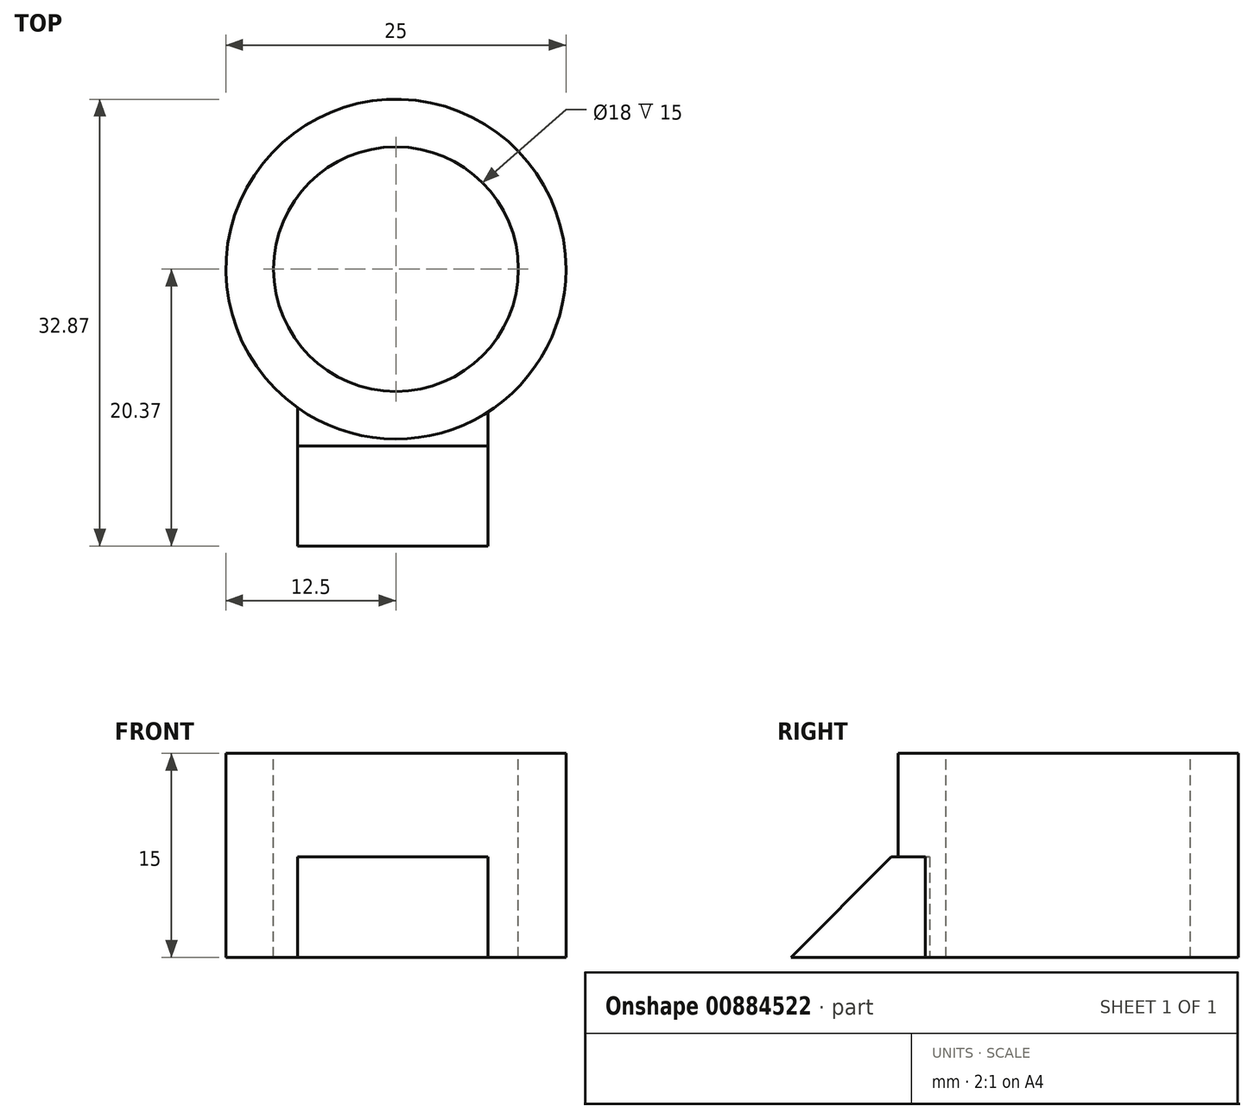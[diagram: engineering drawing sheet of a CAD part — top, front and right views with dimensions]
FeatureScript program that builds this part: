
annotation { "Feature Type Name" : "Feature", "Feature Type Description" : "" }
export const myFeature = defineFeature(function(context is Context, id is Id, definition is map)
    precondition{}
    {
        {
            var Q0;
            Q0=qCreatedBy(makeId("Top.planeOp"),FACE);
            var sketch = newSketch(context, id + "F0", { "sketchPlane" : qUnion([Q0])});
            skCircle(sketch, "E0", {"center": v(0, 0) * mm, "radius": 12.5 * mm});
            skSolve(sketch);
        }
        {
            var Q0;
            Q0 = qSketchRegion(id + "F0", true);
            extrude(context, id + "F1", {"entities" : qUnion([Q0]), "endBound" : BoundingType.SYMMETRIC, "depth" : 15 * mm, "offsetDistance" : 25 * mm});
        }
        {
            var Q0;
            Q0=makeQuery(id+"F1.opExtrude","CAP_FACE",FACE,{"disambiguationData":[OSD([sQuery(id+"F0.wireOp",EDGE,"E0")])],"isStart":false});
            var sketch = newSketch(context, id + "F2", { "sketchPlane" : qUnion([Q0])});
            skCircle(sketch, "E1", {"center": v(0, 0) * mm, "radius": 9 * mm});
            skSolve(sketch);
        }
        {
            var Q0;
            Q0 = qSketchRegion(id + "F2", true);
            extrude(context, id + "F3", {"entities" : qUnion([Q0]), "operationType" : NewBodyOperationType.REMOVE, "oppositeDirection" : true, "depth" : 25 * mm, "offsetDistance" : 25 * mm});
        }
        {
            var Q0;
            Q0=qCreatedBy(makeId("Front.planeOp"),FACE);
            var sketch = newSketch(context, id + "F4", { "sketchPlane" : qUnion([Q0])});
            skLineSegment(sketch, "E2.bottom", {"start": v(-7.23, -0.13) * mm, "end": v(6.77, -0.13) * mm});
            skLineSegment(sketch, "E2.top", {"start": v(-7.23, -7.5) * mm, "end": v(6.77, -7.5) * mm});
            skLineSegment(sketch, "E2.left", {"start": v(-7.23, -0.13) * mm, "end": v(-7.23, -7.5) * mm});
            skLineSegment(sketch, "E2.right", {"start": v(6.77, -0.13) * mm, "end": v(6.77, -7.5) * mm});
            skPoint(sketch, "E2.middle", {"position": v(-0.23, -3.82) * mm});
            skSolve(sketch);
        }
        {
            var Q0;
            Q0 = qSketchRegion(id + "F4", true);
            extrude(context, id + "F5", {"entities" : qUnion([Q0]), "operationType" : NewBodyOperationType.ADD, "depth" : 23 * mm, "offsetDistance" : 25 * mm});
        }
        {
            var Q0;
            Q0=makeQuery(id+"F5.boolean.opBoolean","MERGE",FACE,{"derivedFrom":[makeQuery(id+"F1.opExtrude","CAP_FACE",FACE,{"disambiguationData":[OSD([sQuery(id+"F0.wireOp",EDGE,"E0")])],"isStart":true}),makeQuery(id+"F5.opExtrude","SWEPT_FACE",FACE,{"disambiguationData":[OSD([sQuery(id+"F4.wireOp",EDGE,"E2.top")])]})]});
            var sketch = newSketch(context, id + "F6", { "sketchPlane" : qUnion([Q0])});
            skCircle(sketch, "E3", {"center": v(0, 0) * mm, "radius": 9 * mm});
            skSolve(sketch);
        }
        {
            var Q0;
            Q0 = qSketchRegion(id + "F6", true);
            extrude(context, id + "F7", {"entities" : qUnion([Q0]), "operationType" : NewBodyOperationType.REMOVE, "oppositeDirection" : true, "depth" : 25 * mm, "offsetDistance" : 25 * mm});
        }
        {
            var Q0;
            Q0=makeQuery(id+"F5.opExtrude","CAP_EDGE",EDGE,{"disambiguationData":[OSD([sQuery(id+"F4.wireOp",EDGE,"E2.bottom")])],"isStart":false});
            chamfer(context, id + "F8", {"entities" : qUnion([Q0]), "width" : 10 * mm, "tangentPropagation" : true});
        }
    });
